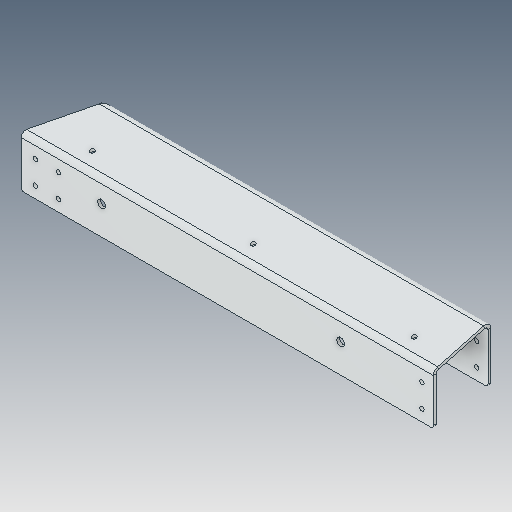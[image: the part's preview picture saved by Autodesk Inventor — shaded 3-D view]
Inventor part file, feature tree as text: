
AUTODESK INVENTOR PART (.ipt)
format: ipt  version: 2023.5 (Build 275446000, 446)  size: 145,408 bytes
history: native  units: in
note: dims shown in document units (in); Inventor stores cm internally (conversion verified against a paired STEP export)
features: fillet x1
ambient origin geometry x8: Origin, YZ Plane, XZ Plane, XY Plane, X Axis, Y Axis, Z Axis, Center Point
bodies: Solid1 (feature_tree)
feature tree (1):
  fillet  "Fillet1"  [1 undecoded]
note: 1 required parameter value undecoded (feature->parameter linkage not recoverable at this tier; creation-order binding heuristic only, values carry confidence <= 0.55)
